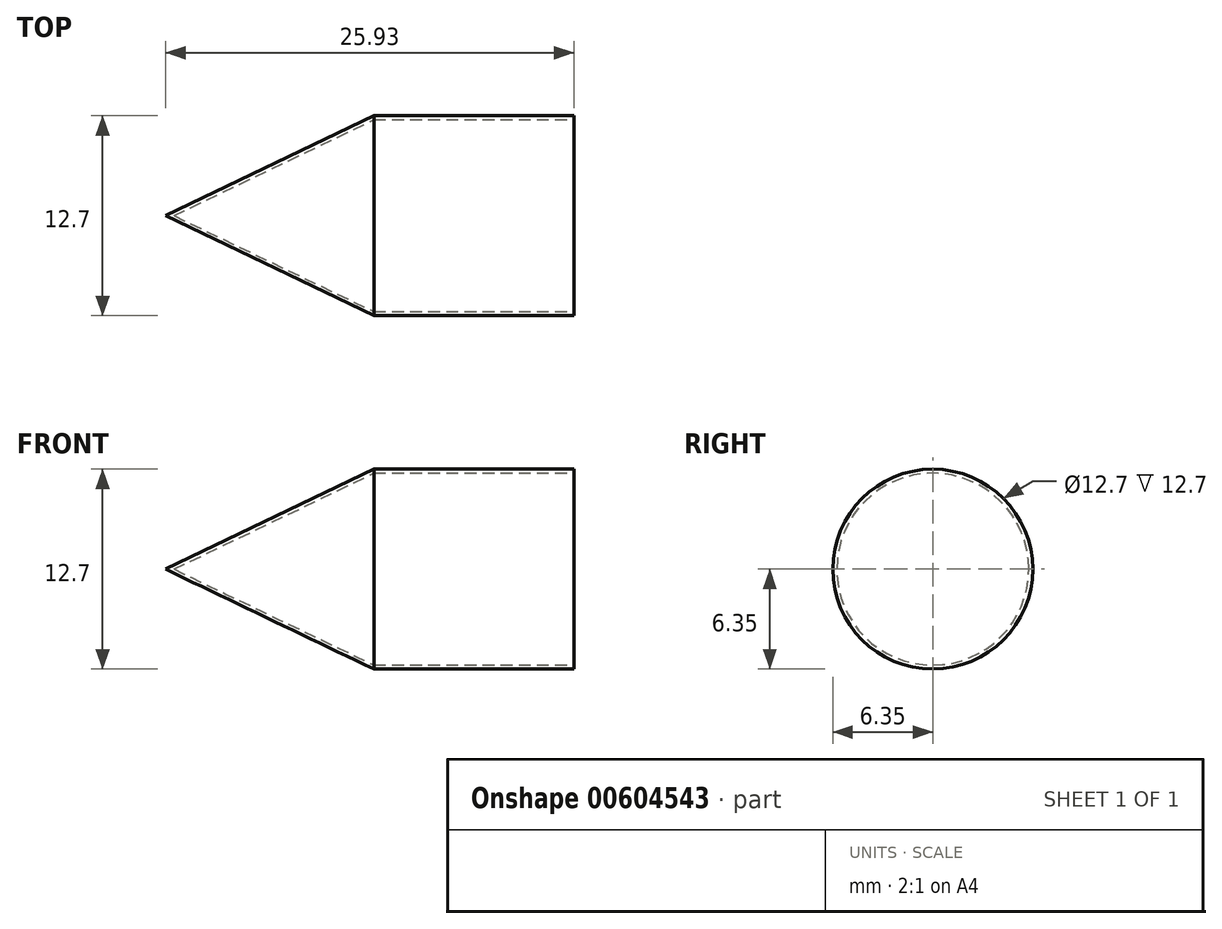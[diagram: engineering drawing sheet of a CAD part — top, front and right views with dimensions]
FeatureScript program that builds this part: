
annotation { "Feature Type Name" : "Feature", "Feature Type Description" : "" }
export const myFeature = defineFeature(function(context is Context, id is Id, definition is map)
    precondition{}
    {
        {
            var Q0;
            Q0=qCreatedBy(makeId("Top.planeOp"),FACE);
            var sketch = newSketch(context, id + "F0", { "sketchPlane" : qUnion([Q0])});
            skLineSegment(sketch, "E0.top", {"start": v(3.02, 6.35) * mm, "end": v(15.72, 6.35) * mm});
            skLineSegment(sketch, "E1", {"start": v(-10.21, 0) * mm, "end": v(3.02, 6.35) * mm});
            skLineSegment(sketch, "E2", {"start": v(-9.68, 0) * mm, "end": v(3.02, 6.1) * mm});
            skLineSegment(sketch, "E3", {"start": v(3.02, 6.1) * mm, "end": v(15.72, 6.1) * mm});
            skLineSegment(sketch, "E4", {"start": v(-2.96, 0) * mm, "end": v(19.26, 0) * mm});
            skLineSegment(sketch, "E5", {"start": v(15.72, 6.35) * mm, "end": v(15.72, 6.1) * mm});
            skSolve(sketch);
        }
        {
            var Q0;
            Q0=sQuery(id+"F0.wireOp",EDGE,"E2");
            var Q1;
            Q1=sQuery(id+"F0.wireOp",EDGE,"E3");
            var Q2;
            Q2=sQuery(id+"F0.wireOp",EDGE,"E0.top");
            var Q3;
            Q3=sQuery(id+"F0.wireOp",EDGE,"E5");
            var Q4;
            Q4=sQuery(id+"F0.wireOp",EDGE,"E1");
            var Q5;
            Q5=sQuery(id+"F0.wireOp",EDGE,"E4");
            revolve(context, id + "F1", {"bodyType" : ToolBodyType.SURFACE, "surfaceEntities" : qUnion([Q0, Q1, Q2, Q3, Q4]), "axis" : qUnion([Q5]), "revolveType" : RevolveType.FULL});
        }
    });
